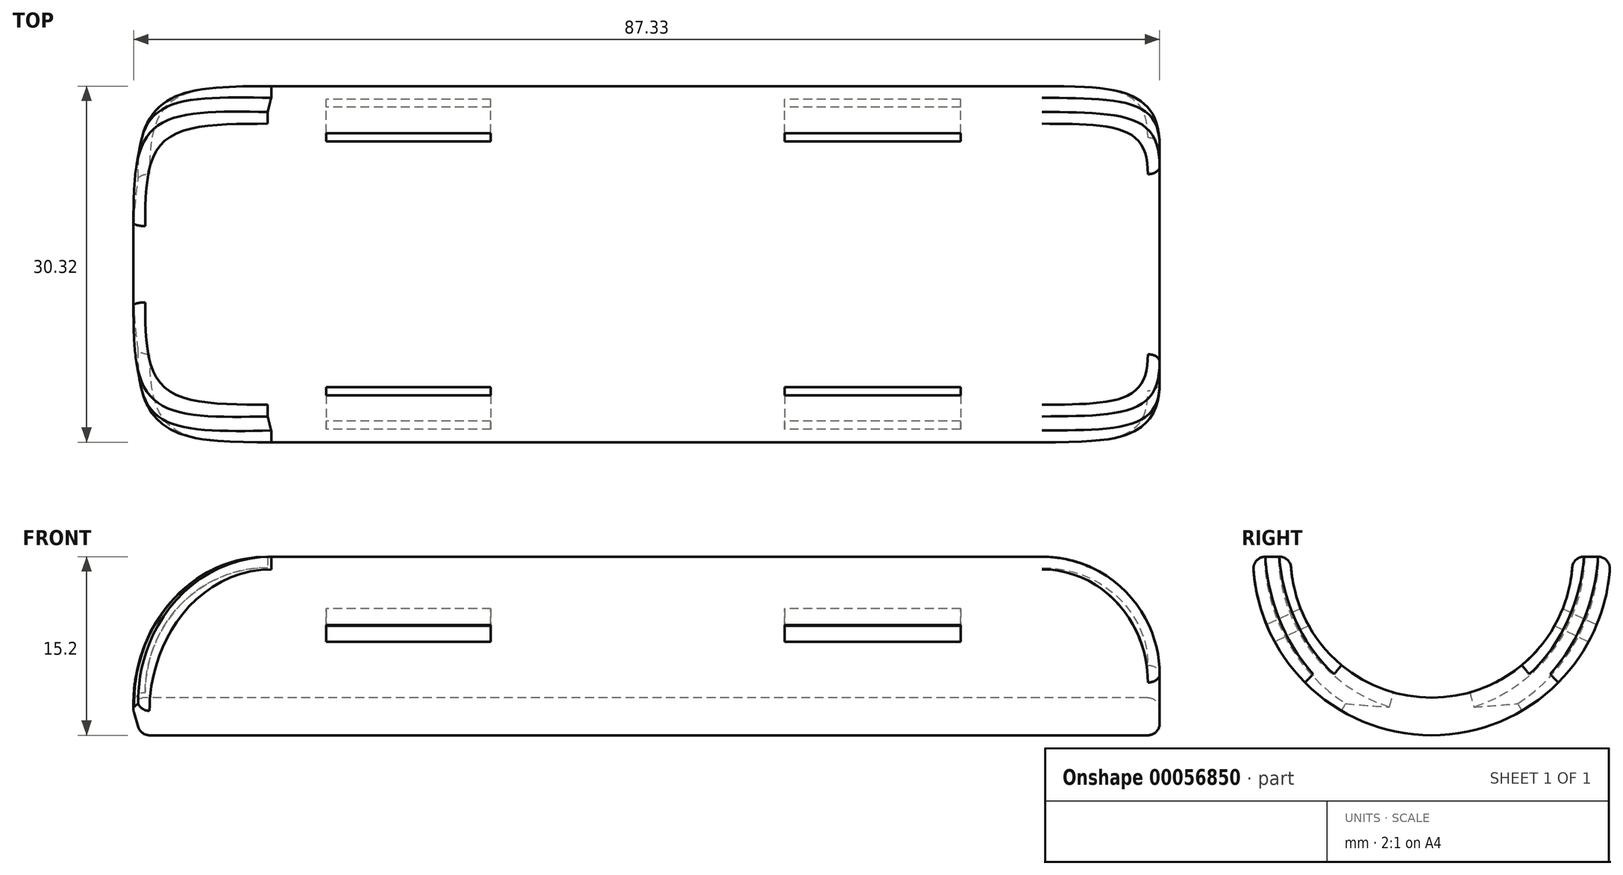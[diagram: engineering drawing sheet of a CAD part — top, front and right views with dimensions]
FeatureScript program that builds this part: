
annotation { "Feature Type Name" : "Feature", "Feature Type Description" : "" }
export const myFeature = defineFeature(function(context is Context, id is Id, definition is map)
    precondition{}
    {
        {
            var Q0;
            Q0=qCreatedBy(makeId("Top.planeOp"),FACE);
            var sketch = newSketch(context, id + "F0", { "sketchPlane" : qUnion([Q0])});
            skLineSegment(sketch, "E0", {"start": v(-26.29, 0) * mm, "end": v(40.92, 0) * mm, "construction": true});
            skLineSegment(sketch, "E1.0", {"start": v(-26.29, -12) * mm, "end": v(40.92, -12) * mm, "construction": true});
            skLineSegment(sketch, "E2.0", {"start": v(-26.29, -15.2) * mm, "end": v(40.92, -15.2) * mm, "construction": true});
            skLineSegment(sketch, "E3", {"start": v(40.92, -12) * mm, "end": v(40.92, -15.2) * mm});
            skLineSegment(sketch, "E4", {"start": v(-19.55, -15.2) * mm, "end": v(40.92, -15.2) * mm});
            skLineSegment(sketch, "E5", {"start": v(40.92, -12) * mm, "end": v(-18.2, -12) * mm});
            skLineSegment(sketch, "E6", {"start": v(-23.84, 0) * mm, "end": v(-22.6, 0) * mm});
            skLineSegment(sketch, "E7.0", {"start": v(70.92, -12) * mm, "end": v(70.92, -15.2) * mm});
            skLineSegment(sketch, "E8", {"start": v(40.92, -12) * mm, "end": v(70.92, -12) * mm});
            skLineSegment(sketch, "E9", {"start": v(40.92, -15.2) * mm, "end": v(70.92, -15.2) * mm});
            skLineSegment(sketch, "E10", {"start": v(-23.84, 0) * mm, "end": v(-26.29, 0) * mm});
            skArc(sketch, "E11.trimOffspring", {"start": v(-21.8, -12) * mm, "mid": v(-20.8, -13.7) * mm, "end": v(-19.55, -15.2) * mm});
            skLineSegment(sketch, "E12", {"start": v(-26.29, 0) * mm, "end": v(-41.3, 0) * mm});
            skArc(sketch, "E13", {"start": v(-31, 0) * mm, "mid": v(-27.1, -8.98) * mm, "end": v(-19.55, -15.2) * mm});
            skArc(sketch, "E14", {"start": v(-29.5, 0) * mm, "mid": v(-25.28, -7.34) * mm, "end": v(-18.2, -12) * mm});
            skArc(sketch, "E15", {"start": v(-28.11, 0) * mm, "mid": v(-26.35, -5.01) * mm, "end": v(-23.16, -9.27) * mm});
            skLineSegment(sketch, "E16", {"start": v(-16.76, -12) * mm, "end": v(-15.8, -15.2) * mm});
            skSolve(sketch);
        }
        {
            var Q0;
            Q0=makeQuery(id+"F0.imprint","IMPRINT",FACE,{"disambiguationData":[TD([[makeQuery(id+"F0.imprint","IMPRINT",EDGE,{"derivedFrom":sQuery(id+"F0.wireOp",EDGE,"E3")}),-1.0]])]});
            var Q1;
            Q1=makeQuery(id+"F0.imprint","IMPRINT",FACE,{"disambiguationData":[TD([[makeQuery(id+"F0.imprint","IMPRINT",EDGE,{"derivedFrom":sQuery(id+"F0.wireOp",EDGE,"E3")}),1.0]])]});
            var Q2;
            Q2=sQuery(id+"F0.wireOp",EDGE,"E0");
            revolve(context, id + "F1", {"entities" : qUnion([Q0, Q1]), "axis" : qUnion([Q2]), "revolveType" : RevolveType.ONE_DIRECTION, "angle" : 180 * degree});
        }
        {
            var Q0;
            Q0=qCreatedBy(makeId("Right.planeOp"),FACE);
            var sketch = newSketch(context, id + "F2", { "sketchPlane" : qUnion([Q0])});
            skArc(sketch, "E17.0.0", {"start": v(11.97, -0.78) * mm, "mid": v(0, -12) * mm, "end": v(-11.97, -0.78) * mm});
            skArc(sketch, "E17.0.2", {"start": v(-7.18, -0.47) * mm, "mid": v(0, -7.2) * mm, "end": v(7.18, -0.47) * mm});
            skArc(sketch, "E18.0.1", {"start": v(-9.28, -0.53) * mm, "mid": v(0, -9.3) * mm, "end": v(9.28, -0.53) * mm});
            skArc(sketch, "E18.0.3", {"start": v(9.28, -0.53) * mm, "mid": v(0, -9.3) * mm, "end": v(-9.28, -0.53) * mm});
            skLineSegment(sketch, "E19", {"start": v(0, 0) * mm, "end": v(-10.49, -5) * mm, "construction": true});
            skLineSegment(sketch, "E20", {"start": v(0, 1.9) * mm, "end": v(0, -13.37) * mm, "construction": true});
            skLineSegment(sketch, "E21.0", {"start": v(-0.34, 0.72) * mm, "end": v(-10.83, -4.27) * mm});
            skLineSegment(sketch, "E22.0", {"start": v(0.34, -0.72) * mm, "end": v(-10.15, -5.72) * mm});
            skLineSegment(sketch, "E23", {"start": v(-9.42, -3.6) * mm, "end": v(-8.73, -5.04) * mm});
            skLineSegment(sketch, "E24", {"start": v(-6.23, -2.08) * mm, "end": v(-5.55, -3.53) * mm});
            skLineSegment(sketch, "E25.MirrorCS", {"start": v(0.34, 0.72) * mm, "end": v(10.83, -4.27) * mm});
            skLineSegment(sketch, "E26.MirrorCS", {"start": v(-0.34, -0.72) * mm, "end": v(10.15, -5.72) * mm});
            skArc(sketch, "E27.0.0", {"start": v(12, 0) * mm, "mid": v(0, -12) * mm, "end": v(-12, 0) * mm});
            skArc(sketch, "E27.0.2", {"start": v(-12, 0) * mm, "mid": v(0, 12) * mm, "end": v(12, 0) * mm});
            skArc(sketch, "E28.0.1", {"start": v(15.2, 0) * mm, "mid": v(0, 15.2) * mm, "end": v(-15.2, 0) * mm});
            skArc(sketch, "E28.0.3", {"start": v(-15.2, 0) * mm, "mid": v(0, -15.2) * mm, "end": v(15.2, 0) * mm});
            skLineSegment(sketch, "E29", {"start": v(-11.15, -4.42) * mm, "end": v(-12.82, -5.22) * mm});
            skLineSegment(sketch, "E30", {"start": v(-10.47, -5.87) * mm, "end": v(-12.13, -6.66) * mm});
            skLineSegment(sketch, "E31", {"start": v(10.83, -4.27) * mm, "end": v(12.91, -5.26) * mm});
            skLineSegment(sketch, "E32", {"start": v(10.15, -5.72) * mm, "end": v(12.19, -6.69) * mm});
            skLineSegment(sketch, "E33", {"start": v(-11.15, -4.42) * mm, "end": v(-20.93, -9.08) * mm});
            skLineSegment(sketch, "E34", {"start": v(-10.47, -5.87) * mm, "end": v(-20.5, -10.65) * mm});
            skLineSegment(sketch, "E35", {"start": v(11.15, -4.42) * mm, "end": v(19.31, -8.3) * mm});
            skLineSegment(sketch, "E36", {"start": v(10.47, -5.87) * mm, "end": v(19.61, -10.22) * mm});
            skSolve(sketch);
        }
        {
            var Q0;
            {var subQ0=sQuery(id+"F2.wireOp",EDGE,"E35");var subQ3=makeQuery(id+"F2.imprint","IMPRINT",VERTEX,{"derivedFrom":subQ0});Q0=makeQuery(id+"F2.imprint","IMPRINT",FACE,{"disambiguationData":[TD([[makeQuery(id+"F2.imprint","IMPRINT",EDGE,{"disambiguationData":[TD([[subQ3,-1.0]])],"derivedFrom":subQ0}),-1.0]])]});}
            var Q1;
            {var subQ0=sQuery(id+"F2.wireOp",EDGE,"E33");var subQ3=makeQuery(id+"F2.imprint","IMPRINT",VERTEX,{"derivedFrom":subQ0});Q1=makeQuery(id+"F2.imprint","IMPRINT",FACE,{"disambiguationData":[TD([[makeQuery(id+"F2.imprint","IMPRINT",EDGE,{"disambiguationData":[TD([[subQ3,1.0]])],"derivedFrom":subQ0}),1.0]])]});}
            extrude(context, id + "F3", {"entities" : qUnion([Q0, Q1]), "operationType" : NewBodyOperationType.REMOVE, "depth" : 14 * mm});
        }
        {
            var Q0;
            Q0=qCreatedBy(makeId("Right.planeOp"),FACE);
            cPlane(context, id + "F4", {"entities" : qUnion([Q0]), "cplaneType" : CPlaneType.OFFSET, "offset" : 39 * mm, "width" : 150 * mm, "height" : 150 * mm});
        }
        {
            var Q0;
            Q0=qCreatedBy(id+"F4.planeOp",FACE);
            var sketch = newSketch(context, id + "F5", { "sketchPlane" : qUnion([Q0])});
            skLineSegment(sketch, "E37.0", {"start": v(6.8, -2.35) * mm, "end": v(8.7, -3.26) * mm});
            skLineSegment(sketch, "E38.0", {"start": v(-0.34, 0.72) * mm, "end": v(-10.83, -4.27) * mm});
            skLineSegment(sketch, "E39.0", {"start": v(-0.34, -0.72) * mm, "end": v(8.02, -4.7) * mm});
            skLineSegment(sketch, "E40.0", {"start": v(0.34, -0.72) * mm, "end": v(-10.15, -5.72) * mm});
            skArc(sketch, "E41.0.0", {"start": v(11.97, -0.78) * mm, "mid": v(0, -12) * mm, "end": v(-11.97, -0.78) * mm});
            skArc(sketch, "E41.0.2", {"start": v(-7.18, -0.47) * mm, "mid": v(0, -7.2) * mm, "end": v(7.18, -0.47) * mm});
            skArc(sketch, "E42.0.1", {"start": v(-9.28, -0.53) * mm, "mid": v(0, -9.3) * mm, "end": v(9.28, -0.53) * mm});
            skArc(sketch, "E42.0.3", {"start": v(9.28, -0.53) * mm, "mid": v(0, -9.3) * mm, "end": v(-9.28, -0.53) * mm});
            skLineSegment(sketch, "E43", {"start": v(6.12, -3.8) * mm, "end": v(8.02, -4.7) * mm});
            skPoint(sketch, "E44.orphan", {"position": v(10.83, -4.27) * mm});
            skPoint(sketch, "E45.orphan", {"position": v(0.34, 0.72) * mm});
            skPoint(sketch, "E46.orphan", {"position": v(10.15, -5.72) * mm});
            skArc(sketch, "E47.0.0", {"start": v(14.07, -5.76) * mm, "mid": v(0, -15.2) * mm, "end": v(-14.07, -5.76) * mm});
            skArc(sketch, "E47.0.1", {"start": v(-14.07, -5.76) * mm, "mid": v(-14.8, -3.3) * mm, "end": v(-15.05, -0.76) * mm});
            skArc(sketch, "E47.0.3", {"start": v(-15.2, 0) * mm, "mid": v(0, -15.2) * mm, "end": v(15.2, 0) * mm});
            skArc(sketch, "E47.0.5", {"start": v(15.05, -0.76) * mm, "mid": v(14.8, -3.3) * mm, "end": v(14.07, -5.76) * mm});
            skLineSegment(sketch, "E48", {"start": v(8.7, -3.26) * mm, "end": v(13.74, -5.65) * mm});
            skLineSegment(sketch, "E49", {"start": v(8.02, -4.7) * mm, "end": v(12.35, -6.77) * mm});
            skLineSegment(sketch, "E50", {"start": v(-10.83, -4.27) * mm, "end": v(-13.1, -5.35) * mm});
            skLineSegment(sketch, "E51", {"start": v(-10.15, -5.72) * mm, "end": v(-13.1, -7.12) * mm});
            skLineSegment(sketch, "E52", {"start": v(11.15, -4.42) * mm, "end": v(16.42, -6.93) * mm});
            skLineSegment(sketch, "E53", {"start": v(10.47, -5.87) * mm, "end": v(17.4, -9.17) * mm});
            skLineSegment(sketch, "E54", {"start": v(-10.15, -5.72) * mm, "end": v(-18.08, -9.5) * mm});
            skLineSegment(sketch, "E55", {"start": v(-10.83, -4.27) * mm, "end": v(-17.08, -7.24) * mm});
            skSolve(sketch);
        }
        {
            var Q0;
            {var subQ0=sQuery(id+"F5.wireOp",EDGE,"E54");var subQ3=makeQuery(id+"F5.imprint","IMPRINT",VERTEX,{"derivedFrom":subQ0});Q0=makeQuery(id+"F5.imprint","IMPRINT",FACE,{"disambiguationData":[TD([[makeQuery(id+"F5.imprint","IMPRINT",EDGE,{"disambiguationData":[TD([[subQ3,1.0]])],"derivedFrom":subQ0}),-1.0]])]});}
            var Q1;
            {var subQ0=sQuery(id+"F5.wireOp",EDGE,"E53");var subQ3=makeQuery(id+"F5.imprint","IMPRINT",VERTEX,{"derivedFrom":subQ0});Q1=makeQuery(id+"F5.imprint","IMPRINT",FACE,{"disambiguationData":[TD([[makeQuery(id+"F5.imprint","IMPRINT",EDGE,{"disambiguationData":[TD([[subQ3,-1.0]])],"derivedFrom":subQ0}),1.0]])]});}
            extrude(context, id + "F6", {"entities" : qUnion([Q0, Q1]), "operationType" : NewBodyOperationType.REMOVE, "depth" : 15 * mm});
        }
        {
            var Q0;
            Q0=makeQuery(id+"F1.opRevolve","SWEPT_EDGE",EDGE,{"disambiguationData":[OSD([sQuery(id+"F0.wireOp",EDGE,"E7.0"),sQuery(id+"F0.wireOp",EDGE,"E8")])]});
            var Q1;
            Q1=makeQuery(id+"F1.opRevolve","SWEPT_EDGE",EDGE,{"disambiguationData":[OSD([sQuery(id+"F0.wireOp",EDGE,"E7.0"),sQuery(id+"F0.wireOp",EDGE,"E9")])]});
            var Q2;
            Q2=makeQuery(id+"F1.opRevolve","CAP_EDGE",EDGE,{"disambiguationData":[OSD([sQuery(id+"F0.wireOp",EDGE,"E4"),sQuery(id+"F0.wireOp",EDGE,"E9")])],"isStart":true});
            var Q3;
            Q3=makeQuery(id+"F1.opRevolve","CAP_EDGE",EDGE,{"disambiguationData":[OSD([sQuery(id+"F0.wireOp",EDGE,"E5"),sQuery(id+"F0.wireOp",EDGE,"E8")])],"isStart":false});
            var Q4;
            Q4=makeQuery(id+"F1.opRevolve","CAP_EDGE",EDGE,{"disambiguationData":[OSD([sQuery(id+"F0.wireOp",EDGE,"E4"),sQuery(id+"F0.wireOp",EDGE,"E9")])],"isStart":false});
            var Q5;
            Q5=makeQuery(id+"F1.opRevolve","CAP_EDGE",EDGE,{"disambiguationData":[OSD([sQuery(id+"F0.wireOp",EDGE,"E5"),sQuery(id+"F0.wireOp",EDGE,"E8")])],"isStart":true});
            var Q6;
            Q6=makeQuery(id+"F1.opRevolve","SWEPT_EDGE",EDGE,{"disambiguationData":[OSD([sQuery(id+"F0.wireOp",EDGE,"E5"),sQuery(id+"F0.wireOp",EDGE,"E16")])]});
            var Q7;
            Q7=makeQuery(id+"F1.opRevolve","SWEPT_EDGE",EDGE,{"disambiguationData":[OSD([sQuery(id+"F0.wireOp",EDGE,"E4"),sQuery(id+"F0.wireOp",EDGE,"E16")])]});
            fillet(context, id + "F7", {"entities" : qUnion([Q0, Q1, Q2, Q3, Q4, Q5, Q6, Q7]), "radius" : 1 * mm, "tangentPropagation" : true, "allowEdgeOverflow" : false});
        }
        {
            var Q0;
            Q0=makeQuery(id+"F1.opRevolve","CAP_EDGE",EDGE,{"disambiguationData":[OSD([sQuery(id+"F0.wireOp",EDGE,"E16")])],"isStart":false});
            var Q1;
            Q1=makeQuery(id+"F1.opRevolve","CAP_EDGE",EDGE,{"disambiguationData":[OSD([sQuery(id+"F0.wireOp",EDGE,"E16")])],"isStart":true});
            var Q2;
            Q2=makeQuery(id+"F1.opRevolve","CAP_EDGE",EDGE,{"disambiguationData":[OSD([sQuery(id+"F0.wireOp",EDGE,"E7.0")])],"isStart":false});
            var Q3;
            Q3=makeQuery(id+"F1.opRevolve","CAP_EDGE",EDGE,{"disambiguationData":[OSD([sQuery(id+"F0.wireOp",EDGE,"E7.0")])],"isStart":true});
            fillet(context, id + "F8", {"entities" : qUnion([Q0, Q1, Q2, Q3]), "radius" : 10 * mm, "tangentPropagation" : true, "allowEdgeOverflow" : false});
        }
    });
